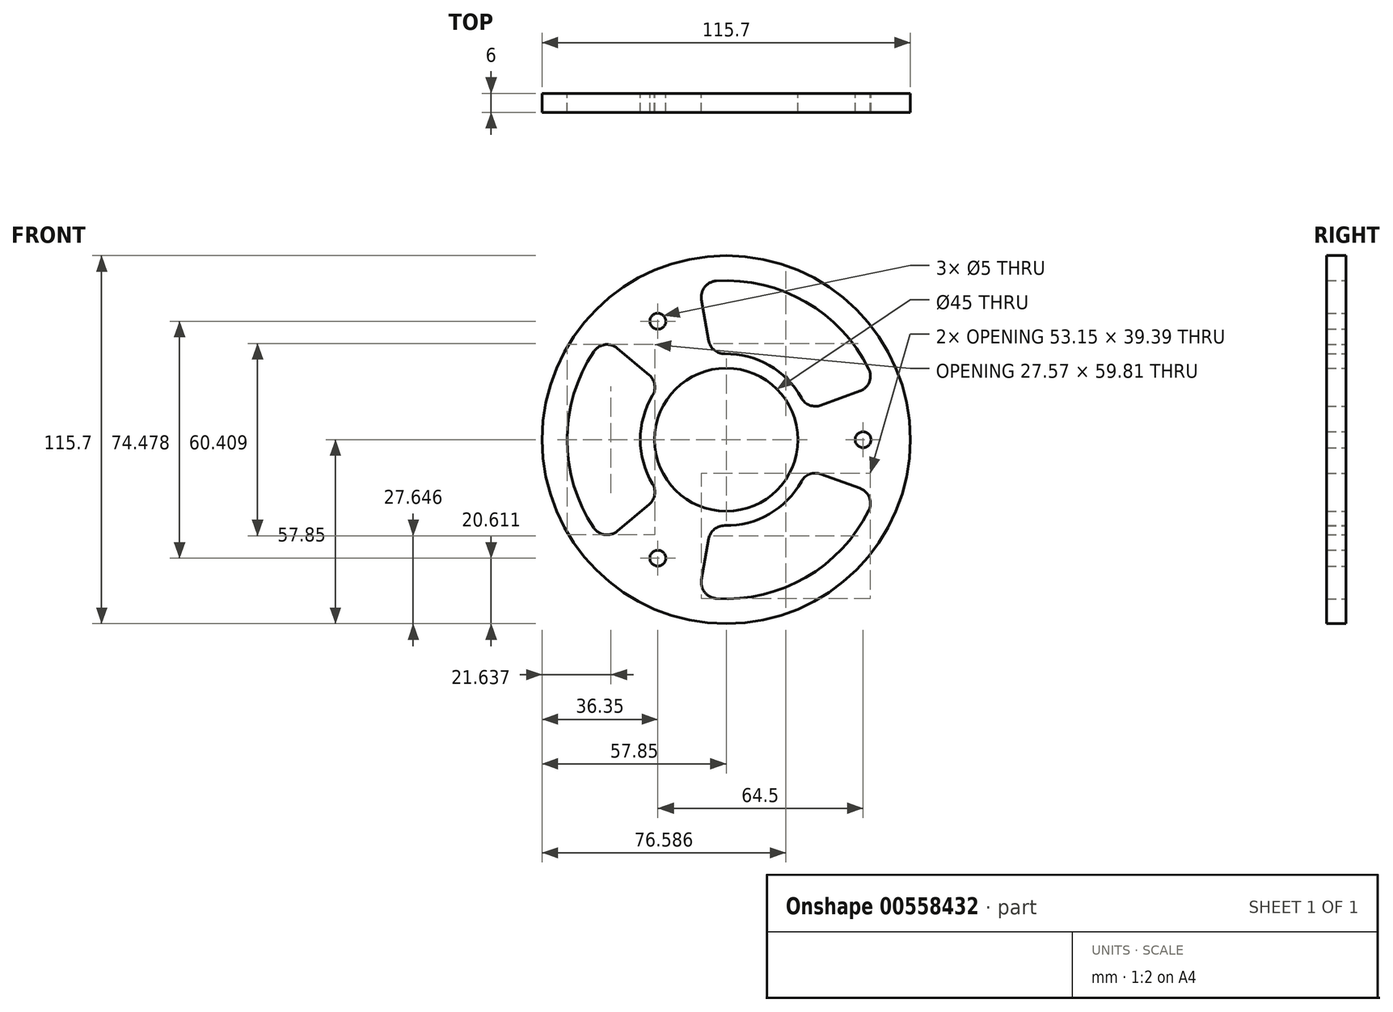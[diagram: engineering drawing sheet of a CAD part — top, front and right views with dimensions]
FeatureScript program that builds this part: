
annotation { "Feature Type Name" : "Feature", "Feature Type Description" : "" }
export const myFeature = defineFeature(function(context is Context, id is Id, definition is map)
    precondition{}
    {
        {
            var Q0;
            Q0=qCreatedBy(makeId("Front.planeOp"),FACE);
            var sketch = newSketch(context, id + "F0", { "sketchPlane" : qUnion([Q0])});
            skCircle(sketch, "E0", {"center": v(0, 0) * mm, "radius": 57.85 * mm});
            skCircle(sketch, "E1", {"center": v(0, 0) * mm, "radius": 22.5 * mm});
            skArc(sketch, "E2", {"start": v(-25.2, 9.68) * mm, "mid": v(-27, 0) * mm, "end": v(-25.2, -9.68) * mm});
            skArc(sketch, "E3", {"start": v(-45.81, 20.03) * mm, "mid": v(-50, 0) * mm, "end": v(-45.81, -20.03) * mm});
            skPoint(sketch, "E4.visualSharp", {"position": v(-23.38, 13.5) * mm});
            skPoint(sketch, "E5.visualSharp", {"position": v(-43.3, 25) * mm});
            skPoint(sketch, "E6.visualSharp", {"position": v(-43.3, -25) * mm});
            skPoint(sketch, "E7.visualSharp", {"position": v(-23.38, -13.5) * mm});
            skPoint(sketch, "E8.MirrorP", {"position": v(23.38, -13.5) * mm});
            skPoint(sketch, "E9.MirrorP", {"position": v(0, -50) * mm});
            skPoint(sketch, "E10.MirrorP", {"position": v(0, -27) * mm});
            skArc(sketch, "E11.MirrorCS", {"start": v(20.99, -16.99) * mm, "mid": v(13.5, -23.38) * mm, "end": v(4.22, -26.67) * mm});
            skArc(sketch, "E12.MirrorCS", {"start": v(40.26, -29.66) * mm, "mid": v(25, -43.3) * mm, "end": v(5.56, -49.7) * mm});
            skArc(sketch, "E13.MirrorCS", {"start": v(4.22, 26.67) * mm, "mid": v(13.5, 23.38) * mm, "end": v(20.99, 16.99) * mm});
            skArc(sketch, "E14.MirrorCS", {"start": v(5.56, 49.7) * mm, "mid": v(25, 43.3) * mm, "end": v(40.26, 29.66) * mm});
            skPoint(sketch, "E15.MirrorP", {"position": v(0, 50) * mm});
            skPoint(sketch, "E16.MirrorP", {"position": v(43.3, 25) * mm});
            skCircle(sketch, "E17", {"center": v(43, 0) * mm, "radius": 2.5 * mm});
            skCircle(sketch, "E18.MirrorC", {"center": v(-21.5, 37.24) * mm, "radius": 2.5 * mm});
            skCircle(sketch, "E19.MirrorC", {"center": v(-21.5, -37.24) * mm, "radius": 2.5 * mm});
            skArc(sketch, "E20", {"start": v(20.99, 16.99) * mm, "mid": v(11.41, 24.47) * mm, "end": v(-0.48, 27) * mm});
            skArc(sketch, "E21", {"start": v(-45.81, 20.03) * mm, "mid": v(-49.92, -2.78) * mm, "end": v(-43.3, -25) * mm});
            skArc(sketch, "E22.trimOffspring", {"start": v(0, -50) * mm, "mid": v(22.55, -44.63) * mm, "end": v(40.26, -29.66) * mm});
            skArc(sketch, "E23.trimOffspring", {"start": v(40.26, 29.66) * mm, "mid": v(21.13, 45.32) * mm, "end": v(-3.16, 49.9) * mm});
            skLineSegment(sketch, "E24.trimOffspring", {"start": v(-10.05, 56.97) * mm, "end": v(-12, 68.06) * mm});
            skLineSegment(sketch, "E25.trimOffspring", {"start": v(-5.49, 31.13) * mm, "end": v(-7.77, 44.04) * mm});
            skLineSegment(sketch, "E26", {"start": v(-24.21, 20.32) * mm, "end": v(-34.26, 28.75) * mm});
            skArc(sketch, "E27", {"start": v(0, -27) * mm, "mid": v(13.5, -23.38) * mm, "end": v(23.38, -13.5) * mm});
            skArc(sketch, "E28.trimOffspring", {"start": v(40.26, 29.66) * mm, "mid": v(18.58, 46.42) * mm, "end": v(-8.68, 49.24) * mm});
            skArc(sketch, "E29.trimOffspring", {"start": v(-23.14, 13.91) * mm, "mid": v(-27, 0.24) * mm, "end": v(-23.38, -13.5) * mm});
            skArc(sketch, "E30.trimOffspring", {"start": v(-41.64, 27.68) * mm, "mid": v(-49.98, 1.58) * mm, "end": v(-43.3, -25) * mm});
            skArc(sketch, "E31.MirrorCS", {"start": v(-41.64, -27.68) * mm, "mid": v(-49.98, -1.58) * mm, "end": v(-43.3, 25) * mm});
            skArc(sketch, "E32.MirrorCS", {"start": v(-23.14, -13.91) * mm, "mid": v(-27, -0.24) * mm, "end": v(-23.38, 13.5) * mm});
            skLineSegment(sketch, "E33.MirrorCS", {"start": v(-24.21, -20.32) * mm, "end": v(-34.26, -28.75) * mm});
            skArc(sketch, "E34.MirrorCS", {"start": v(5.56, 49.7) * mm, "mid": v(28.68, 40.96) * mm, "end": v(44.8, 22.22) * mm});
            skLineSegment(sketch, "E35.MirrorCS", {"start": v(29.7, 10.81) * mm, "end": v(42.02, 15.3) * mm});
            skArc(sketch, "E36.MirrorCS", {"start": v(20.99, 16.99) * mm, "mid": v(13.5, 23.38) * mm, "end": v(4.22, 26.67) * mm});
            skArc(sketch, "E37.MirrorCS", {"start": v(4.22, 26.67) * mm, "mid": v(15.49, 22.12) * mm, "end": v(23.62, 13.09) * mm});
            skLineSegment(sketch, "E38", {"start": v(0, 0) * mm, "end": v(119.14, 0) * mm});
            skLineSegment(sketch, "E39.MirrorCS", {"start": v(29.7, -10.81) * mm, "end": v(42.02, -15.3) * mm});
            skArc(sketch, "E40.MirrorCS", {"start": v(4.22, -26.67) * mm, "mid": v(15.49, -22.12) * mm, "end": v(23.62, -13.09) * mm});
            skArc(sketch, "E41.MirrorCS", {"start": v(5.56, -49.7) * mm, "mid": v(28.68, -40.96) * mm, "end": v(44.8, -22.22) * mm});
            skLineSegment(sketch, "E42.MirrorCS", {"start": v(-5.49, -31.13) * mm, "end": v(-7.77, -44.04) * mm});
            skArc(sketch, "E43.MirrorCS", {"start": v(-3.16, -49.9) * mm, "mid": v(23.62, -44.07) * mm, "end": v(43.3, -25) * mm});
            skArc(sketch, "E44.MirrorCS", {"start": v(-0.48, -27) * mm, "mid": v(13.3, -23.5) * mm, "end": v(23.38, -13.5) * mm});
            skPoint(sketch, "E45.visualSharp", {"position": v(-38.3, -32.14) * mm});
            skArc(sketch, "E45.filletArc", {"start": v(-41.64, -27.68) * mm, "mid": v(-38.18, -29.87) * mm, "end": v(-34.26, -28.75) * mm});
            skPoint(sketch, "E46.visualSharp", {"position": v(-38.3, 32.14) * mm});
            skArc(sketch, "E46.filletArc", {"start": v(-34.26, 28.75) * mm, "mid": v(-38.18, 29.87) * mm, "end": v(-41.64, 27.68) * mm});
            skPoint(sketch, "E47.visualSharp", {"position": v(-20.68, 17.36) * mm});
            skArc(sketch, "E47.filletArc", {"start": v(-23.14, 13.91) * mm, "mid": v(-22.5, 17.31) * mm, "end": v(-24.21, 20.32) * mm});
            skPoint(sketch, "E48.visualSharp", {"position": v(-20.68, -17.36) * mm});
            skArc(sketch, "E48.filletArc", {"start": v(-24.21, -20.32) * mm, "mid": v(-22.5, -17.31) * mm, "end": v(-23.14, -13.91) * mm});
            skPoint(sketch, "E49.visualSharp", {"position": v(-4.69, -26.59) * mm});
            skArc(sketch, "E49.filletArc", {"start": v(-0.48, -27) * mm, "mid": v(-3.74, -28.14) * mm, "end": v(-5.49, -31.13) * mm});
            skPoint(sketch, "E50.visualSharp", {"position": v(-8.68, -49.24) * mm});
            skArc(sketch, "E50.filletArc", {"start": v(-7.77, -44.04) * mm, "mid": v(-6.77, -48) * mm, "end": v(-3.16, -49.9) * mm});
            skPoint(sketch, "E51.visualSharp", {"position": v(46.98, -17.1) * mm});
            skArc(sketch, "E51.filletArc", {"start": v(44.8, -22.22) * mm, "mid": v(44.96, -18.14) * mm, "end": v(42.02, -15.3) * mm});
            skPoint(sketch, "E52.visualSharp", {"position": v(25.37, -9.23) * mm});
            skArc(sketch, "E52.filletArc", {"start": v(29.7, -10.81) * mm, "mid": v(26.24, -10.83) * mm, "end": v(23.62, -13.09) * mm});
            skPoint(sketch, "E53.visualSharp", {"position": v(46.98, 17.1) * mm});
            skArc(sketch, "E53.filletArc", {"start": v(42.02, 15.3) * mm, "mid": v(44.96, 18.14) * mm, "end": v(44.8, 22.22) * mm});
            skPoint(sketch, "E54.visualSharp", {"position": v(25.37, 9.23) * mm});
            skArc(sketch, "E54.filletArc", {"start": v(23.62, 13.09) * mm, "mid": v(26.24, 10.83) * mm, "end": v(29.7, 10.81) * mm});
            skPoint(sketch, "E55.visualSharp", {"position": v(-4.69, 26.59) * mm});
            skArc(sketch, "E55.filletArc", {"start": v(-5.49, 31.13) * mm, "mid": v(-3.74, 28.14) * mm, "end": v(-0.48, 27) * mm});
            skPoint(sketch, "E56.visualSharp", {"position": v(-8.68, 49.24) * mm});
            skArc(sketch, "E56.filletArc", {"start": v(-3.16, 49.9) * mm, "mid": v(-6.77, 48) * mm, "end": v(-7.77, 44.04) * mm});
            skSolve(sketch);
        }
        {
            var Q0;
            Q0=makeQuery(id+"F0.imprint","IMPRINT",FACE,{"disambiguationData":[TD([[makeQuery(id+"F0.imprint","IMPRINT",EDGE,{"derivedFrom":sQuery(id+"F0.wireOp",EDGE,"E0")}),1.0]])]});
            extrude(context, id + "F1", {"entities" : qUnion([Q0]), "depth" : 6 * mm, "offsetDistance" : 25 * mm});
        }
    });
